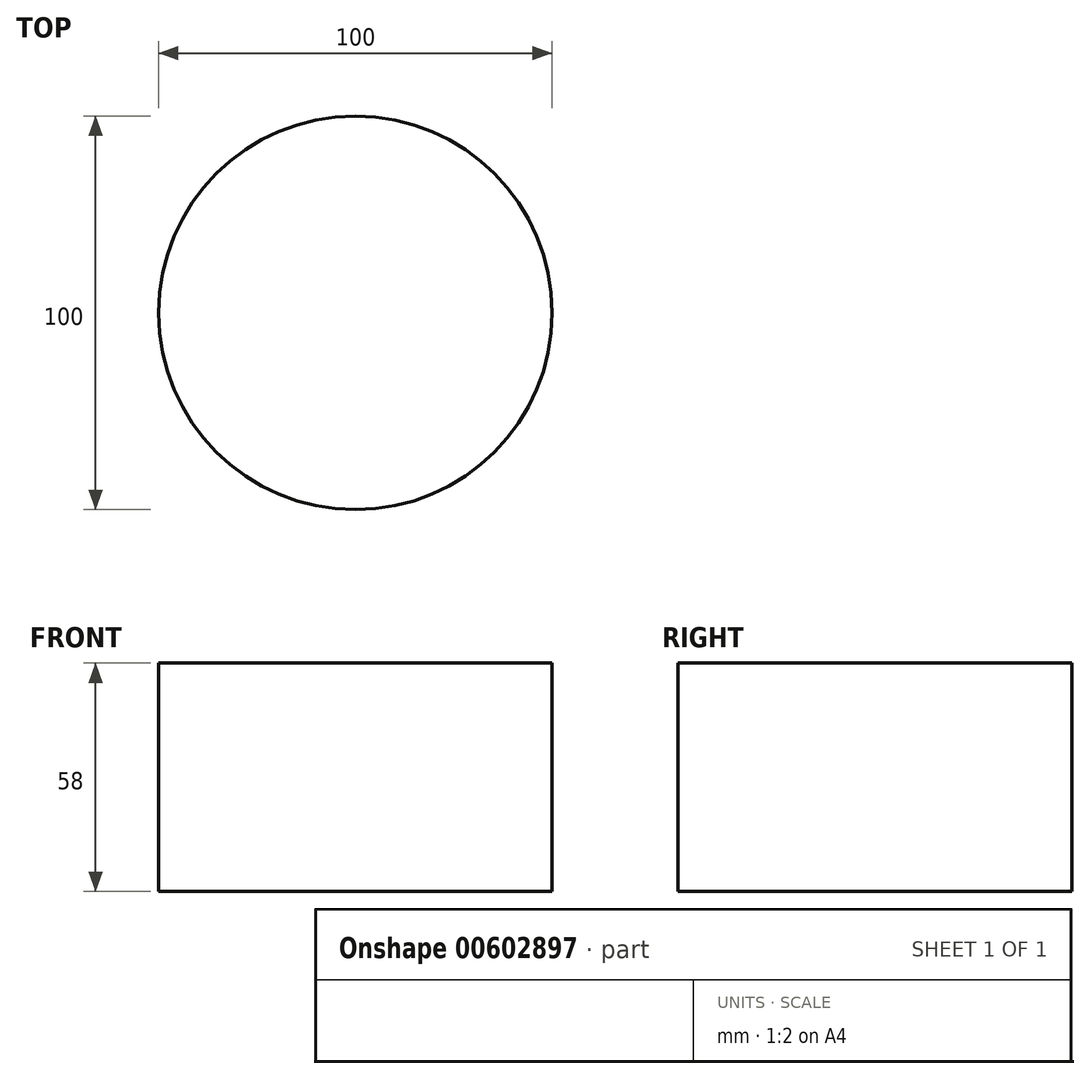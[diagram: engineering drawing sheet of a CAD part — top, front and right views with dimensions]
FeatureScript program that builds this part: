
annotation { "Feature Type Name" : "Feature", "Feature Type Description" : "" }
export const myFeature = defineFeature(function(context is Context, id is Id, definition is map)
    precondition{}
    {
        {
            var Q0;
            Q0=qCreatedBy(makeId("Top.planeOp"),FACE);
            var sketch = newSketch(context, id + "F0", { "sketchPlane" : qUnion([Q0])});
            skCircle(sketch, "E0", {"center": v(0, 0) * mm, "radius": 50 * mm});
            skSolve(sketch);
        }
        {
            var Q0;
            Q0 = qSketchRegion(id + "F0", true);
            extrude(context, id + "F1", {"entities" : qUnion([Q0]), "depth" : 58 * mm, "offsetDistance" : 25 * mm});
        }
    });
